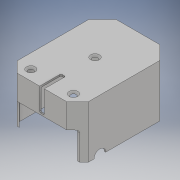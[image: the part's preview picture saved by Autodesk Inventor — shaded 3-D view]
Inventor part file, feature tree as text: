
AUTODESK INVENTOR PART (.ipt)
format: ipt  version: 2017 (Build 210142000, 142)  size: 461,312 bytes
history: native  units: mm
features: extrude x9, sketch x7, other x6, fillet x4, hole x3, projected_geometry x1
ambient origin geometry x8: Origin, YZ Plane, XZ Plane, XY Plane, X Axis, Y Axis, Z Axis, Center Point
bodies: Body1 (feature_tree)
feature tree (30):
  other  "Твердое тело1"
  sketch  "Эскиз1"
  extrude  "Выдавливание1"  Depth=58.6mm
  extrude  "Выдавливание2"  Depth=80.0mm
  fillet  "Сопряжение1"  Radius=11.0mm
  extrude  "Выдавливание3"  Depth=11.0mm
  extrude  "Выдавливание4"  Depth=8.5mm
  extrude  "Выдавливание5"  Depth=8.5mm
  other  "Комбинировать1"
  hole  "Отверстие4"  [1 undecoded]
  hole  "Отверстие5"  [1 undecoded]
  hole  "Отверстие6"  [1 undecoded]
  fillet  "Сопряжение2"  Radius=11.0mm
  fillet  "Сопряжение3"  Radius=1.2mm
  extrude  "Выдавливание6"  Depth=1.5mm TaperAngle=0.0deg
  extrude  "Выдавливание7"  Depth=43.5mm TaperAngle=0.0deg
  extrude  "Выдавливание8"  Depth=1.0mm
  other  "Комбинировать2"
  fillet  "Сопряжение4"  Radius=4.0mm
  other  "РабПлоскость1"
  extrude  "Выдавливание11"  Depth=17.0mm
  other  "Твердое тело2"
  sketch  "Эскиз2"
  sketch  "Эскиз3"
  sketch  "Эскиз4"
  other  "Твердое тело3"
  sketch  "Эскиз5"
  sketch  "Эскиз6"
  sketch  "Эскиз9"
  projected_geometry  "Спроецированная петля1"
note: 3 required parameter values undecoded (feature->parameter linkage not recoverable at this tier; creation-order binding heuristic only, values carry confidence <= 0.55)
